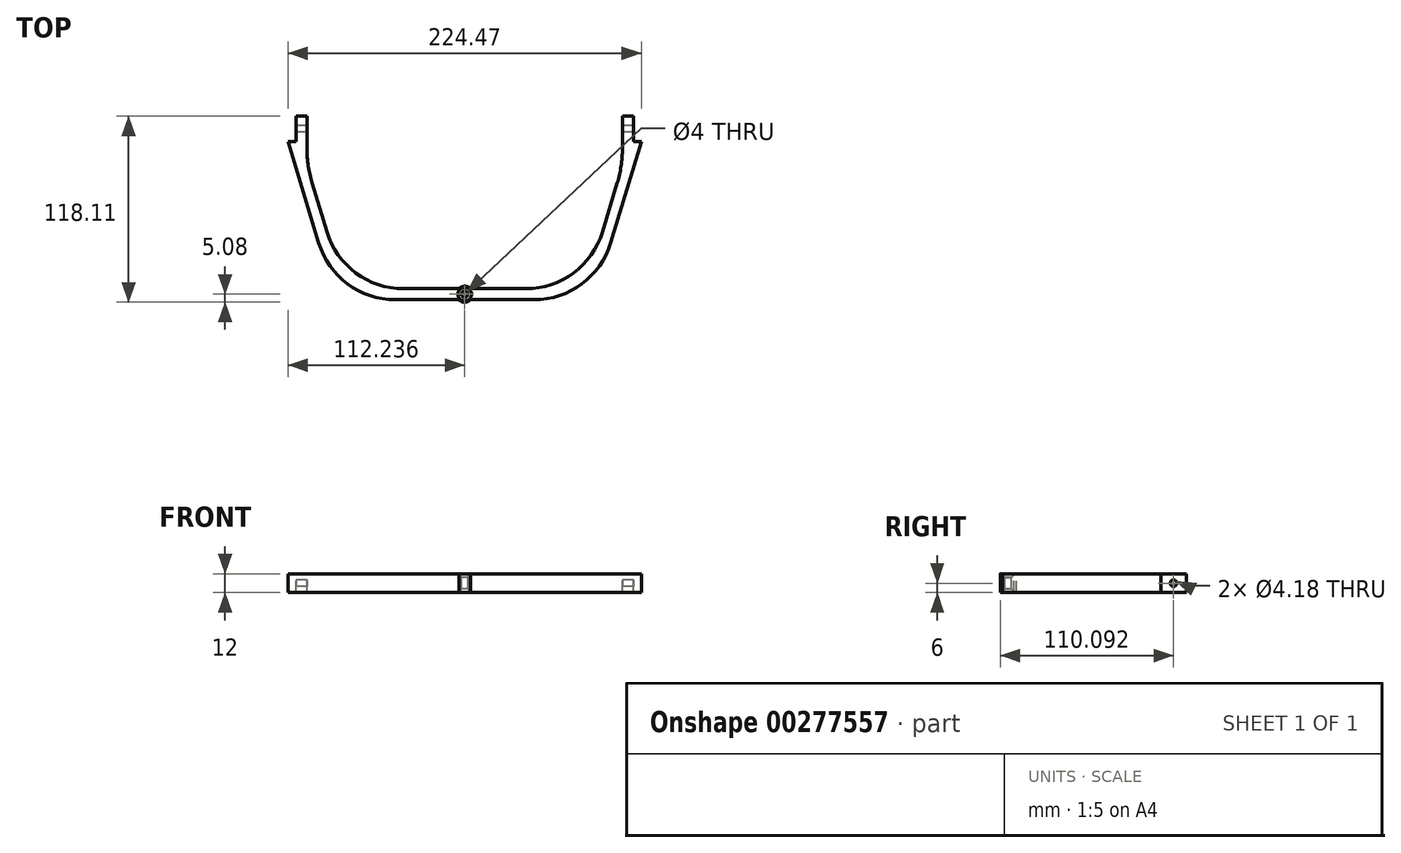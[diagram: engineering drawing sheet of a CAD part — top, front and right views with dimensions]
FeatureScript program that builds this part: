
annotation { "Feature Type Name" : "Feature", "Feature Type Description" : "" }
export const myFeature = defineFeature(function(context is Context, id is Id, definition is map)
    precondition{}
    {
        {
            var Q0;
            Q0=qCreatedBy(makeId("Top.planeOp"),FACE);
            var sketch = newSketch(context, id + "F0", { "sketchPlane" : qUnion([Q0])});
            skLineSegment(sketch, "E0.left", {"start": v(0, 0) * mm, "end": v(0, 140) * mm, "construction": true});
            skLineSegment(sketch, "E1", {"start": v(5.08, 0) * mm, "end": v(5.08, 140) * mm, "construction": true});
            skLineSegment(sketch, "E2.top", {"start": v(5.08, 118.1) * mm, "end": v(12.08, 118.1) * mm});
            skCircle(sketch, "E3", {"center": v(112.24, 5.08) * mm, "radius": 5.08 * mm});
            skPoint(sketch, "E3.centerSnap0", {"position": v(112.24, 0) * mm});
            skCircle(sketch, "E4", {"center": v(112.24, 5.08) * mm, "radius": 2 * mm});
            skLineSegment(sketch, "E5", {"start": v(5.08, 102.07) * mm, "end": v(0, 102.07) * mm});
            skLineSegment(sketch, "E6", {"start": v(0, 102.07) * mm, "end": v(19.54, 37.64) * mm});
            skLineSegment(sketch, "E7", {"start": v(12.08, 118.11) * mm, "end": v(12.08, 97.66) * mm});
            skLineSegment(sketch, "E8", {"start": v(15.36, 75.55) * mm, "end": v(24.73, 44.64) * mm});
            skLineSegment(sketch, "E9", {"start": v(108.55, 8.58) * mm, "end": v(73.35, 8.58) * mm});
            skLineSegment(sketch, "E10", {"start": v(68.15, 1.58) * mm, "end": v(108.55, 1.58) * mm});
            skLineSegment(sketch, "E11", {"start": v(5.08, 118.1) * mm, "end": v(5.08, 102.07) * mm});
            skPoint(sketch, "E12.orphan", {"position": v(38.27, 0) * mm});
            skPoint(sketch, "E13.visualSharp", {"position": v(35.67, 8.58) * mm});
            skArc(sketch, "E13.filletArc", {"start": v(24.73, 44.64) * mm, "mid": v(43.08, 18.58) * mm, "end": v(73.35, 8.58) * mm});
            skArc(sketch, "E14.filletArc", {"start": v(19.54, 37.64) * mm, "mid": v(37.89, 11.58) * mm, "end": v(68.15, 1.58) * mm});
            skLineSegment(sketch, "E15", {"start": v(112.24, 5.08) * mm, "end": v(112.24, 64.13) * mm, "construction": true});
            skLineSegment(sketch, "E16.MirrorCS", {"start": v(115.92, 8.58) * mm, "end": v(151.13, 8.58) * mm});
            skLineSegment(sketch, "E17.MirrorCS", {"start": v(156.32, 1.58) * mm, "end": v(115.92, 1.58) * mm});
            skArc(sketch, "E18.MirrorCS", {"start": v(204.93, 37.64) * mm, "mid": v(186.58, 11.58) * mm, "end": v(156.32, 1.58) * mm});
            skArc(sketch, "E19.MirrorCS", {"start": v(199.74, 44.64) * mm, "mid": v(181.4, 18.58) * mm, "end": v(151.13, 8.58) * mm});
            skLineSegment(sketch, "E20.MirrorCS", {"start": v(209.11, 75.55) * mm, "end": v(199.74, 44.64) * mm});
            skLineSegment(sketch, "E21.MirrorCS", {"start": v(224.47, 102.07) * mm, "end": v(204.93, 37.64) * mm});
            skLineSegment(sketch, "E22.MirrorCS", {"start": v(219.4, 102.07) * mm, "end": v(224.47, 102.07) * mm});
            skLineSegment(sketch, "E23.MirrorCS", {"start": v(219.4, 118.1) * mm, "end": v(219.4, 102.07) * mm});
            skLineSegment(sketch, "E24.MirrorCS", {"start": v(212.4, 118.11) * mm, "end": v(212.4, 97.66) * mm});
            skLineSegment(sketch, "E25.MirrorCS", {"start": v(219.4, 118.1) * mm, "end": v(212.4, 118.1) * mm});
            skPoint(sketch, "E26.visualSharp", {"position": v(12.08, 86.36) * mm});
            skArc(sketch, "E26.filletArc", {"start": v(12.08, 97.66) * mm, "mid": v(12.9, 86.48) * mm, "end": v(15.36, 75.55) * mm});
            skPoint(sketch, "E27.visualSharp", {"position": v(212.4, 86.36) * mm});
            skArc(sketch, "E27.filletArc", {"start": v(209.11, 75.55) * mm, "mid": v(211.57, 86.48) * mm, "end": v(212.4, 97.66) * mm});
            skSolve(sketch);
        }
        {
            var Q0;
            Q0 = qSketchRegion(id + "F0", true);
            extrude(context, id + "F1", {"entities" : qUnion([Q0]), "oppositeDirection" : true, "depth" : 12 * mm});
        }
        {
            var Q0;
            Q0=makeQuery(id+"F1.opExtrude","CAP_EDGE",EDGE,{"disambiguationData":[OSD([sQuery(id+"F0.wireOp",EDGE,"E4")])],"isStart":true});
            chamfer(context, id + "F2", {"entities" : qUnion([Q0]), "width" : 2.3 * mm, "tangentPropagation" : true});
        }
        {
            var Q0;
            Q0=makeQuery(id+"F1.opExtrude","CAP_EDGE",EDGE,{"disambiguationData":[OSD([sQuery(id+"F0.wireOp",EDGE,"E4")])],"isStart":false});
            chamfer(context, id + "F3", {"entities" : qUnion([Q0]), "width" : 2.3 * mm, "tangentPropagation" : true});
        }
        {
            var Q0;
            Q0=makeQuery(id+"F1.opExtrude","SWEPT_FACE",FACE,{"disambiguationData":[OSD([sQuery(id+"F0.wireOp",EDGE,"E11")])]});
            var sketch = newSketch(context, id + "F4", { "sketchPlane" : qUnion([Q0])});
            skCircle(sketch, "E28", {"center": v(-110.1, -6) * mm, "radius": 2.09 * mm});
            skPoint(sketch, "E28.centerSnap0", {"position": v(-118.1, -6) * mm});
            skPoint(sketch, "E28.centerSnap1", {"position": v(-110.1, 0) * mm});
            skSolve(sketch);
        }
        {
            var Q0;
            Q0 = qSketchRegion(id + "F4", true);
            extrude(context, id + "F5", {"entities" : qUnion([Q0]), "operationType" : NewBodyOperationType.REMOVE, "endBound" : BoundingType.THROUGH_ALL, "oppositeDirection" : true, "depth" : 25.4 * mm});
        }
    });
